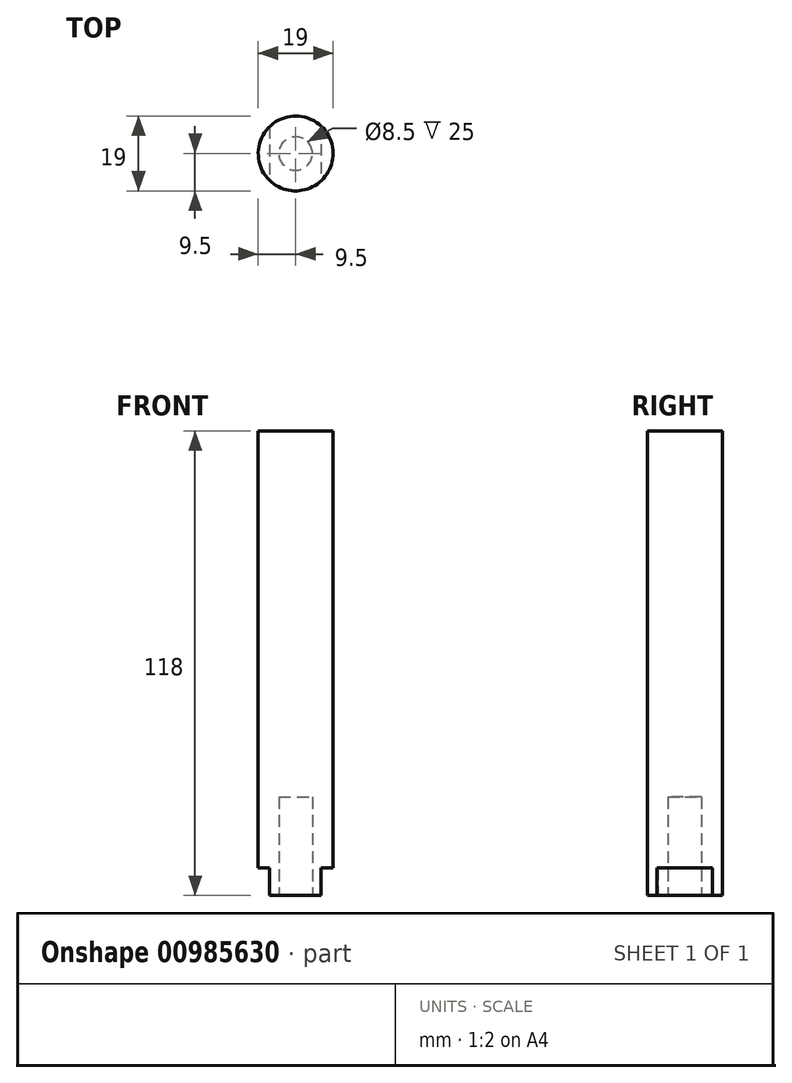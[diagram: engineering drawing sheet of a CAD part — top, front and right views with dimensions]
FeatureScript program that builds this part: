
annotation { "Feature Type Name" : "Feature", "Feature Type Description" : "" }
export const myFeature = defineFeature(function(context is Context, id is Id, definition is map)
    precondition{}
    {
        {
            var Q0;
            Q0=qCreatedBy(makeId("Top.planeOp"),FACE);
            var sketch = newSketch(context, id + "F0", { "sketchPlane" : qUnion([Q0])});
            skCircle(sketch, "E0", {"center": v(0, 0) * mm, "radius": 9.5 * mm});
            skSolve(sketch);
        }
        {
            var Q0;
            Q0 = qSketchRegion(id + "F0", true);
            extrude(context, id + "F1", {"entities" : qUnion([Q0]), "depth" : 118 * mm, "offsetDistance" : 25 * mm});
        }
        {
            var Q0;
            Q0=qCreatedBy(makeId("Front.planeOp"),FACE);
            var sketch = newSketch(context, id + "F2", { "sketchPlane" : qUnion([Q0])});
            skLineSegment(sketch, "E1.bottom", {"start": v(-6.62, 7) * mm, "end": v(-16.13, 7) * mm});
            skLineSegment(sketch, "E1.top", {"start": v(-6.62, -7) * mm, "end": v(-16.13, -7) * mm});
            skLineSegment(sketch, "E1.left", {"start": v(-6.62, 7) * mm, "end": v(-6.62, -7) * mm});
            skLineSegment(sketch, "E1.right", {"start": v(-16.13, 7) * mm, "end": v(-16.13, -7) * mm});
            skPoint(sketch, "E1.middle", {"position": v(-11.37, 0) * mm});
            skLineSegment(sketch, "E2.bottom", {"start": v(6.38, 7) * mm, "end": v(16.66, 7) * mm});
            skLineSegment(sketch, "E2.top", {"start": v(6.38, -7) * mm, "end": v(16.66, -7) * mm});
            skLineSegment(sketch, "E2.left", {"start": v(6.38, 7) * mm, "end": v(6.38, -7) * mm});
            skLineSegment(sketch, "E2.right", {"start": v(16.66, 7) * mm, "end": v(16.66, -7) * mm});
            skPoint(sketch, "E2.middle", {"position": v(11.52, 0) * mm});
            skSolve(sketch);
        }
        {
            var Q0;
            Q0 = qSketchRegion(id + "F2", true);
            extrude(context, id + "F3", {"entities" : qUnion([Q0]), "operationType" : NewBodyOperationType.REMOVE, "endBound" : BoundingType.SYMMETRIC, "oppositeDirection" : true, "depth" : 25 * mm, "offsetDistance" : 25 * mm});
        }
        {
            var Q0;
            Q0=makeQuery(id+"F1.opExtrude","CAP_FACE",FACE,{"disambiguationData":[OSD([sQuery(id+"F0.wireOp",EDGE,"E0")])],"isStart":true});
            var sketch = newSketch(context, id + "F4", { "sketchPlane" : qUnion([Q0])});
            skCircle(sketch, "E3", {"center": v(0, 0) * mm, "radius": 4.25 * mm});
            skSolve(sketch);
        }
        {
            var Q0;
            Q0 = qSketchRegion(id + "F4", true);
            extrude(context, id + "F5", {"entities" : qUnion([Q0]), "operationType" : NewBodyOperationType.REMOVE, "oppositeDirection" : true, "depth" : 25 * mm, "offsetDistance" : 25 * mm});
        }
    });
